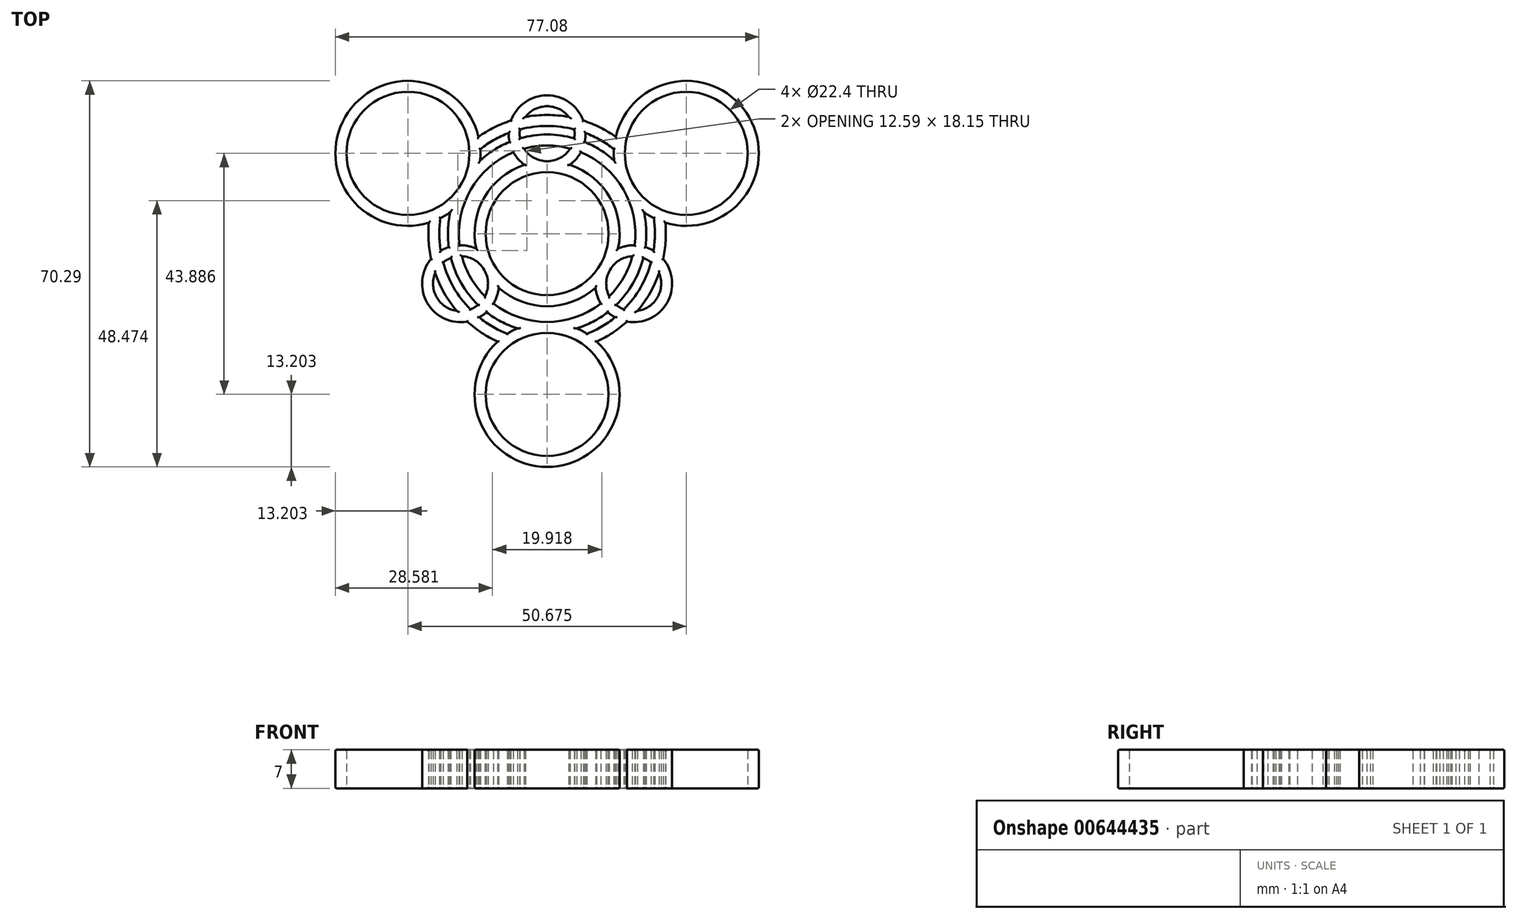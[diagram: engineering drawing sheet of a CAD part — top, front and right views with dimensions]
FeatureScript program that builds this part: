
annotation { "Feature Type Name" : "Feature", "Feature Type Description" : "" }
export const myFeature = defineFeature(function(context is Context, id is Id, definition is map)
    precondition{}
    {
        {
            var Q0;
            Q0=qCreatedBy(makeId("Top.planeOp"),FACE);
            var sketch = newSketch(context, id + "F0", { "sketchPlane" : qUnion([Q0])});
            skCircle(sketch, "E0", {"center": v(0, 0) * mm, "radius": 11.2 * mm});
            skArc(sketch, "E1.0", {"start": v(-4.12, 12.54) * mm, "mid": v(-11.43, 6.6) * mm, "end": v(-12.92, -2.7) * mm});
            skArc(sketch, "E2", {"start": v(4.93, 17.37) * mm, "mid": v(5, 18.18) * mm, "end": v(4.94, 18.99) * mm});
            skArc(sketch, "E3.0", {"start": v(4.12, 12.54) * mm, "mid": v(5.26, 13.58) * mm, "end": v(6.14, 14.84) * mm});
            skPoint(sketch, "E4", {"position": v(0, 11.2) * mm});
            skArc(sketch, "E5.1.0", {"start": v(8.8, -9.84) * mm, "mid": v(9.13, -11.34) * mm, "end": v(9.78, -12.74) * mm});
            skArc(sketch, "E5.1.1", {"start": v(12.58, -12.96) * mm, "mid": v(13.24, -13.42) * mm, "end": v(13.97, -13.77) * mm});
            skArc(sketch, "E5.2.0", {"start": v(-12.92, -2.7) * mm, "mid": v(-14.39, -2.24) * mm, "end": v(-15.92, -2.1) * mm});
            skArc(sketch, "E5.2.1", {"start": v(-17.5, -4.42) * mm, "mid": v(-18.24, -4.76) * mm, "end": v(-18.91, -5.22) * mm});
            skLineSegment(sketch, "E5.anchor1", {"start": v(0, 0) * mm, "end": v(0, 18.2) * mm, "construction": true});
            skLineSegment(sketch, "E5.anchor2", {"start": v(0, 0) * mm, "end": v(-15.76, -9.1) * mm, "construction": true});
            skArc(sketch, "E6", {"start": v(-15.52, -4.1) * mm, "mid": v(-13.9, -8.03) * mm, "end": v(-11.32, -11.4) * mm});
            skArc(sketch, "E7.0", {"start": v(12.2, 13.3) * mm, "mid": v(9.67, 15.25) * mm, "end": v(6.84, 16.71) * mm});
            skArc(sketch, "E8.trimOffspring", {"start": v(12.92, -2.7) * mm, "mid": v(11.43, 6.6) * mm, "end": v(4.12, 12.54) * mm});
            skArc(sketch, "E9.trimOffspring", {"start": v(-8.8, -9.84) * mm, "mid": v(0, -13.2) * mm, "end": v(8.8, -9.84) * mm});
            skArc(sketch, "E10.trimOffspring", {"start": v(6.84, 16.71) * mm, "mid": v(6.97, 17.51) * mm, "end": v(7, 18.33) * mm});
            skArc(sketch, "E11.trimOffspring", {"start": v(-4.2, 15.5) * mm, "mid": v(0, 13.2) * mm, "end": v(4.2, 15.5) * mm});
            skArc(sketch, "E12.trimOffspring", {"start": v(-6.14, 14.84) * mm, "mid": v(-5.26, 13.58) * mm, "end": v(-4.12, 12.54) * mm});
            skArc(sketch, "E13.trimOffspring", {"start": v(-17.9, -2.43) * mm, "mid": v(-18.65, -2.72) * mm, "end": v(-19.37, -3.1) * mm});
            skArc(sketch, "E14.trimOffspring", {"start": v(-9.78, -12.74) * mm, "mid": v(-9.13, -11.34) * mm, "end": v(-8.8, -9.84) * mm});
            skArc(sketch, "E15.trimOffspring", {"start": v(-11.32, -11.4) * mm, "mid": v(-11.43, -6.6) * mm, "end": v(-15.52, -4.1) * mm});
            skArc(sketch, "E16.trimOffspring", {"start": v(11.05, -14.28) * mm, "mid": v(11.68, -14.8) * mm, "end": v(12.37, -15.22) * mm});
            skArc(sketch, "E17.trimOffspring", {"start": v(15.52, -4.1) * mm, "mid": v(11.43, -6.6) * mm, "end": v(11.32, -11.4) * mm});
            skArc(sketch, "E18.trimOffspring", {"start": v(15.92, -2.1) * mm, "mid": v(14.39, -2.24) * mm, "end": v(12.92, -2.7) * mm});
            skCircle(sketch, "E19", {"center": v(25.34, 14.63) * mm, "radius": 11.2 * mm});
            skArc(sketch, "E20.0", {"start": v(21.53, 2) * mm, "mid": v(36.77, 21.23) * mm, "end": v(12.49, 17.65) * mm});
            skLineSegment(sketch, "E21", {"start": v(25.34, 14.63) * mm, "end": v(25.34, 1.43) * mm, "construction": true});
            skLineSegment(sketch, "E22", {"start": v(25.34, 14.63) * mm, "end": v(13.9, 8.03) * mm, "construction": true});
            skLineSegment(sketch, "E23", {"start": v(0, 0) * mm, "end": v(13.9, 8.03) * mm, "construction": true});
            skCircle(sketch, "E24.1.0", {"center": v(-25.34, 14.63) * mm, "radius": 11.2 * mm});
            skArc(sketch, "E24.1.1", {"start": v(-19.41, 2.83) * mm, "mid": v(-18.5, 3.34) * mm, "end": v(-17.63, 3.91) * mm});
            skCircle(sketch, "E24.2.0", {"center": v(0, -29.26) * mm, "radius": 11.2 * mm});
            skArc(sketch, "E24.2.1", {"start": v(7.25, -18.23) * mm, "mid": v(6.36, -17.69) * mm, "end": v(5.42, -17.22) * mm});
            skArc(sketch, "E25", {"start": v(12.16, 15.4) * mm, "mid": v(9.7, 17.06) * mm, "end": v(7, 18.33) * mm});
            skArc(sketch, "E26.0", {"start": v(12.49, 17.65) * mm, "mid": v(9.65, 19.35) * mm, "end": v(6.58, 20.6) * mm});
            skArc(sketch, "E27.trimOffspring", {"start": v(12.16, 15.4) * mm, "mid": v(12.14, 14.35) * mm, "end": v(12.2, 13.3) * mm});
            skArc(sketch, "E28.trimOffspring", {"start": v(17.63, 3.91) * mm, "mid": v(18.5, 3.34) * mm, "end": v(19.41, 2.83) * mm});
            skArc(sketch, "E29.trimOffspring", {"start": v(19.37, -3.1) * mm, "mid": v(18.65, -2.72) * mm, "end": v(17.9, -2.43) * mm});
            skArc(sketch, "E30.trimOffspring", {"start": v(18.91, -5.22) * mm, "mid": v(18.24, -4.76) * mm, "end": v(17.5, -4.42) * mm});
            skArc(sketch, "E31.trimOffspring", {"start": v(16.42, -14.06) * mm, "mid": v(20.1, -11.6) * mm, "end": v(20.38, -7.2) * mm});
            skArc(sketch, "E32.trimOffspring", {"start": v(14.54, -16) * mm, "mid": v(21.82, -12.6) * mm, "end": v(21.12, -4.6) * mm});
            skArc(sketch, "E33.trimOffspring", {"start": v(6.58, 20.6) * mm, "mid": v(0, 25.2) * mm, "end": v(-6.58, 20.6) * mm});
            skArc(sketch, "E34.trimOffspring", {"start": v(3.96, 21.25) * mm, "mid": v(0, 23.2) * mm, "end": v(-3.96, 21.25) * mm});
            skArc(sketch, "E35.trimOffspring", {"start": v(-4.94, 18.99) * mm, "mid": v(-5, 18.18) * mm, "end": v(-4.93, 17.37) * mm});
            skArc(sketch, "E36.trimOffspring", {"start": v(-7, 18.33) * mm, "mid": v(-6.97, 17.51) * mm, "end": v(-6.84, 16.71) * mm});
            skArc(sketch, "E37.trimOffspring", {"start": v(-12.37, -15.22) * mm, "mid": v(-11.68, -14.8) * mm, "end": v(-11.05, -14.28) * mm});
            skArc(sketch, "E38.trimOffspring", {"start": v(-13.97, -13.77) * mm, "mid": v(-13.24, -13.42) * mm, "end": v(-12.58, -12.96) * mm});
            skArc(sketch, "E39.trimOffspring", {"start": v(-20.38, -7.2) * mm, "mid": v(-20.1, -11.6) * mm, "end": v(-16.42, -14.06) * mm});
            skArc(sketch, "E40.trimOffspring", {"start": v(-21.12, -4.6) * mm, "mid": v(-21.82, -12.6) * mm, "end": v(-14.54, -16) * mm});
            skArc(sketch, "E41.trimOffspring", {"start": v(-21.53, 2) * mm, "mid": v(-21.58, -1.32) * mm, "end": v(-21.12, -4.6) * mm});
            skArc(sketch, "E42.trimOffspring", {"start": v(-19.41, 2.83) * mm, "mid": v(-19.62, -0.14) * mm, "end": v(-19.37, -3.1) * mm});
            skArc(sketch, "E43.trimOffspring", {"start": v(9.04, -19.64) * mm, "mid": v(11.93, -18.03) * mm, "end": v(14.54, -16) * mm});
            skArc(sketch, "E44.trimOffspring", {"start": v(7.25, -18.23) * mm, "mid": v(9.93, -16.92) * mm, "end": v(12.37, -15.22) * mm});
            skArc(sketch, "E45.trimOffspring", {"start": v(5.42, -17.22) * mm, "mid": v(8.37, -16) * mm, "end": v(11.05, -14.28) * mm});
            skArc(sketch, "E46.trimOffspring", {"start": v(-9.04, -19.64) * mm, "mid": v(0, -42.46) * mm, "end": v(9.04, -19.64) * mm});
            skArc(sketch, "E47.trimOffspring", {"start": v(-5.42, -17.22) * mm, "mid": v(-6.36, -17.69) * mm, "end": v(-7.25, -18.23) * mm});
            skArc(sketch, "E48.trimOffspring", {"start": v(-12.49, 17.65) * mm, "mid": v(-36.77, 21.23) * mm, "end": v(-21.53, 2) * mm});
            skArc(sketch, "E49.trimOffspring", {"start": v(-17.63, 3.91) * mm, "mid": v(-18.04, 0.75) * mm, "end": v(-17.9, -2.43) * mm});
            skArc(sketch, "E50.trimOffspring", {"start": v(-12.2, 13.3) * mm, "mid": v(-12.14, 14.35) * mm, "end": v(-12.16, 15.4) * mm});
            skArc(sketch, "E51.trimOffspring", {"start": v(-17.5, -4.42) * mm, "mid": v(-15.64, -9.03) * mm, "end": v(-12.58, -12.96) * mm});
            skArc(sketch, "E52.trimOffspring", {"start": v(-18.91, -5.22) * mm, "mid": v(-16.99, -9.8) * mm, "end": v(-13.97, -13.77) * mm});
            skArc(sketch, "E53.trimOffspring", {"start": v(-20.38, -7.2) * mm, "mid": v(-18.72, -10.8) * mm, "end": v(-16.42, -14.06) * mm});
            skArc(sketch, "E54.trimOffspring", {"start": v(-14.54, -16) * mm, "mid": v(-11.93, -18.03) * mm, "end": v(-9.04, -19.64) * mm});
            skArc(sketch, "E55.trimOffspring", {"start": v(-12.37, -15.22) * mm, "mid": v(-9.93, -16.92) * mm, "end": v(-7.25, -18.23) * mm});
            skArc(sketch, "E56.trimOffspring", {"start": v(-11.05, -14.28) * mm, "mid": v(-8.37, -16) * mm, "end": v(-5.42, -17.22) * mm});
            skArc(sketch, "E57.trimOffspring", {"start": v(-9.78, -12.74) * mm, "mid": v(0, -16.06) * mm, "end": v(9.78, -12.74) * mm});
            skArc(sketch, "E58.trimOffspring", {"start": v(11.32, -11.4) * mm, "mid": v(13.9, -8.03) * mm, "end": v(15.52, -4.1) * mm});
            skArc(sketch, "E59.trimOffspring", {"start": v(12.58, -12.96) * mm, "mid": v(15.64, -9.03) * mm, "end": v(17.5, -4.42) * mm});
            skArc(sketch, "E60.trimOffspring", {"start": v(13.97, -13.77) * mm, "mid": v(16.99, -9.8) * mm, "end": v(18.91, -5.22) * mm});
            skArc(sketch, "E61.trimOffspring", {"start": v(16.42, -14.06) * mm, "mid": v(18.72, -10.8) * mm, "end": v(20.38, -7.2) * mm});
            skArc(sketch, "E62.trimOffspring", {"start": v(21.12, -4.6) * mm, "mid": v(21.58, -1.32) * mm, "end": v(21.53, 2) * mm});
            skArc(sketch, "E63.trimOffspring", {"start": v(19.37, -3.1) * mm, "mid": v(19.62, -0.14) * mm, "end": v(19.41, 2.83) * mm});
            skArc(sketch, "E64.trimOffspring", {"start": v(17.9, -2.43) * mm, "mid": v(18.04, 0.75) * mm, "end": v(17.63, 3.91) * mm});
            skArc(sketch, "E65.trimOffspring", {"start": v(15.92, -2.1) * mm, "mid": v(13.9, 8.03) * mm, "end": v(6.14, 14.84) * mm});
            skArc(sketch, "E66.trimOffspring", {"start": v(-6.14, 14.84) * mm, "mid": v(-13.9, 8.03) * mm, "end": v(-15.92, -2.1) * mm});
            skArc(sketch, "E67.trimOffspring", {"start": v(-6.84, 16.71) * mm, "mid": v(-9.67, 15.25) * mm, "end": v(-12.2, 13.3) * mm});
            skArc(sketch, "E68.trimOffspring", {"start": v(-7, 18.33) * mm, "mid": v(-9.7, 17.06) * mm, "end": v(-12.16, 15.4) * mm});
            skArc(sketch, "E69.trimOffspring", {"start": v(-6.58, 20.6) * mm, "mid": v(-9.65, 19.35) * mm, "end": v(-12.49, 17.65) * mm});
            skArc(sketch, "E70.trimOffspring", {"start": v(3.96, 21.25) * mm, "mid": v(0, 21.62) * mm, "end": v(-3.96, 21.25) * mm});
            skArc(sketch, "E71.trimOffspring", {"start": v(4.94, 18.99) * mm, "mid": v(0, 19.62) * mm, "end": v(-4.94, 18.99) * mm});
            skArc(sketch, "E72.trimOffspring", {"start": v(4.93, 17.37) * mm, "mid": v(0, 18.06) * mm, "end": v(-4.93, 17.37) * mm});
            skArc(sketch, "E73.trimOffspring", {"start": v(4.2, 15.5) * mm, "mid": v(0, 16.06) * mm, "end": v(-4.2, 15.5) * mm});
            skSolve(sketch);
        }
        {
            var Q0;
            Q0=makeQuery(id+"F0.imprint","IMPRINT",FACE,{"disambiguationData":[TD([[makeQuery(id+"F0.imprint","IMPRINT",EDGE,{"derivedFrom":sQuery(id+"F0.wireOp",EDGE,"E0")}),-1.0]])]});
            extrude(context, id + "F1", {"entities" : qUnion([Q0]), "depth" : 7 * mm, "offsetDistance" : 25 * mm});
        }
        {
            var Q0;
            Q0=makeQuery(id+"F1.opExtrude","CAP_FACE",FACE,{"disambiguationData":[OSD([sQuery(id+"F0.wireOp",EDGE,"E0"),sQuery(id+"F0.wireOp",EDGE,"E1.0"),sQuery(id+"F0.wireOp",EDGE,"E2"),sQuery(id+"F0.wireOp",EDGE,"E3.0"),sQuery(id+"F0.wireOp",EDGE,"E5.1.0"),sQuery(id+"F0.wireOp",EDGE,"E5.1.1"),sQuery(id+"F0.wireOp",EDGE,"E5.2.0"),sQuery(id+"F0.wireOp",EDGE,"E5.2.1"),sQuery(id+"F0.wireOp",EDGE,"E6"),sQuery(id+"F0.wireOp",EDGE,"E7.0"),sQuery(id+"F0.wireOp",EDGE,"E8.trimOffspring"),sQuery(id+"F0.wireOp",EDGE,"E9.trimOffspring"),sQuery(id+"F0.wireOp",EDGE,"E10.trimOffspring"),sQuery(id+"F0.wireOp",EDGE,"E11.trimOffspring"),sQuery(id+"F0.wireOp",EDGE,"E12.trimOffspring"),sQuery(id+"F0.wireOp",EDGE,"E13.trimOffspring"),sQuery(id+"F0.wireOp",EDGE,"E14.trimOffspring"),sQuery(id+"F0.wireOp",EDGE,"E15.trimOffspring"),sQuery(id+"F0.wireOp",EDGE,"E16.trimOffspring"),sQuery(id+"F0.wireOp",EDGE,"E17.trimOffspring"),sQuery(id+"F0.wireOp",EDGE,"E18.trimOffspring"),sQuery(id+"F0.wireOp",EDGE,"E19"),sQuery(id+"F0.wireOp",EDGE,"E20.0"),sQuery(id+"F0.wireOp",EDGE,"E24.1.0"),sQuery(id+"F0.wireOp",EDGE,"E24.1.1"),sQuery(id+"F0.wireOp",EDGE,"E24.2.0"),sQuery(id+"F0.wireOp",EDGE,"E24.2.1"),sQuery(id+"F0.wireOp",EDGE,"E25"),sQuery(id+"F0.wireOp",EDGE,"E26.0"),sQuery(id+"F0.wireOp",EDGE,"E27.trimOffspring"),sQuery(id+"F0.wireOp",EDGE,"E28.trimOffspring"),sQuery(id+"F0.wireOp",EDGE,"E29.trimOffspring"),sQuery(id+"F0.wireOp",EDGE,"E30.trimOffspring"),sQuery(id+"F0.wireOp",EDGE,"E31.trimOffspring"),sQuery(id+"F0.wireOp",EDGE,"E32.trimOffspring"),sQuery(id+"F0.wireOp",EDGE,"E33.trimOffspring"),sQuery(id+"F0.wireOp",EDGE,"E34.trimOffspring"),sQuery(id+"F0.wireOp",EDGE,"E35.trimOffspring"),sQuery(id+"F0.wireOp",EDGE,"E36.trimOffspring"),sQuery(id+"F0.wireOp",EDGE,"E37.trimOffspring"),sQuery(id+"F0.wireOp",EDGE,"E38.trimOffspring"),sQuery(id+"F0.wireOp",EDGE,"E39.trimOffspring"),sQuery(id+"F0.wireOp",EDGE,"E40.trimOffspring"),sQuery(id+"F0.wireOp",EDGE,"E41.trimOffspring"),sQuery(id+"F0.wireOp",EDGE,"E42.trimOffspring"),sQuery(id+"F0.wireOp",EDGE,"E43.trimOffspring"),sQuery(id+"F0.wireOp",EDGE,"E44.trimOffspring"),sQuery(id+"F0.wireOp",EDGE,"E45.trimOffspring"),sQuery(id+"F0.wireOp",EDGE,"E46.trimOffspring"),sQuery(id+"F0.wireOp",EDGE,"E47.trimOffspring"),sQuery(id+"F0.wireOp",EDGE,"E48.trimOffspring"),sQuery(id+"F0.wireOp",EDGE,"E49.trimOffspring"),sQuery(id+"F0.wireOp",EDGE,"E50.trimOffspring"),sQuery(id+"F0.wireOp",EDGE,"E51.trimOffspring"),sQuery(id+"F0.wireOp",EDGE,"E52.trimOffspring"),sQuery(id+"F0.wireOp",EDGE,"E53.trimOffspring"),sQuery(id+"F0.wireOp",EDGE,"E54.trimOffspring"),sQuery(id+"F0.wireOp",EDGE,"E55.trimOffspring"),sQuery(id+"F0.wireOp",EDGE,"E56.trimOffspring"),sQuery(id+"F0.wireOp",EDGE,"E57.trimOffspring"),sQuery(id+"F0.wireOp",EDGE,"E58.trimOffspring"),sQuery(id+"F0.wireOp",EDGE,"E59.trimOffspring"),sQuery(id+"F0.wireOp",EDGE,"E60.trimOffspring"),sQuery(id+"F0.wireOp",EDGE,"E61.trimOffspring"),sQuery(id+"F0.wireOp",EDGE,"E62.trimOffspring"),sQuery(id+"F0.wireOp",EDGE,"E63.trimOffspring"),sQuery(id+"F0.wireOp",EDGE,"E64.trimOffspring"),sQuery(id+"F0.wireOp",EDGE,"E65.trimOffspring"),sQuery(id+"F0.wireOp",EDGE,"E66.trimOffspring"),sQuery(id+"F0.wireOp",EDGE,"E67.trimOffspring"),sQuery(id+"F0.wireOp",EDGE,"E68.trimOffspring"),sQuery(id+"F0.wireOp",EDGE,"E69.trimOffspring"),sQuery(id+"F0.wireOp",EDGE,"E70.trimOffspring"),sQuery(id+"F0.wireOp",EDGE,"E71.trimOffspring"),sQuery(id+"F0.wireOp",EDGE,"E72.trimOffspring"),sQuery(id+"F0.wireOp",EDGE,"E73.trimOffspring")])],"isStart":false});
            var Q1;
            Q1=makeQuery(id+"F1.opExtrude","CAP_FACE",FACE,{"disambiguationData":[OSD([sQuery(id+"F0.wireOp",EDGE,"E0"),sQuery(id+"F0.wireOp",EDGE,"E1.0"),sQuery(id+"F0.wireOp",EDGE,"E2"),sQuery(id+"F0.wireOp",EDGE,"E3.0"),sQuery(id+"F0.wireOp",EDGE,"E5.1.0"),sQuery(id+"F0.wireOp",EDGE,"E5.1.1"),sQuery(id+"F0.wireOp",EDGE,"E5.2.0"),sQuery(id+"F0.wireOp",EDGE,"E5.2.1"),sQuery(id+"F0.wireOp",EDGE,"E6"),sQuery(id+"F0.wireOp",EDGE,"E7.0"),sQuery(id+"F0.wireOp",EDGE,"E8.trimOffspring"),sQuery(id+"F0.wireOp",EDGE,"E9.trimOffspring"),sQuery(id+"F0.wireOp",EDGE,"E10.trimOffspring"),sQuery(id+"F0.wireOp",EDGE,"E11.trimOffspring"),sQuery(id+"F0.wireOp",EDGE,"E12.trimOffspring"),sQuery(id+"F0.wireOp",EDGE,"E13.trimOffspring"),sQuery(id+"F0.wireOp",EDGE,"E14.trimOffspring"),sQuery(id+"F0.wireOp",EDGE,"E15.trimOffspring"),sQuery(id+"F0.wireOp",EDGE,"E16.trimOffspring"),sQuery(id+"F0.wireOp",EDGE,"E17.trimOffspring"),sQuery(id+"F0.wireOp",EDGE,"E18.trimOffspring"),sQuery(id+"F0.wireOp",EDGE,"E19"),sQuery(id+"F0.wireOp",EDGE,"E20.0"),sQuery(id+"F0.wireOp",EDGE,"E24.1.0"),sQuery(id+"F0.wireOp",EDGE,"E24.1.1"),sQuery(id+"F0.wireOp",EDGE,"E24.2.0"),sQuery(id+"F0.wireOp",EDGE,"E24.2.1"),sQuery(id+"F0.wireOp",EDGE,"E25"),sQuery(id+"F0.wireOp",EDGE,"E26.0"),sQuery(id+"F0.wireOp",EDGE,"E27.trimOffspring"),sQuery(id+"F0.wireOp",EDGE,"E28.trimOffspring"),sQuery(id+"F0.wireOp",EDGE,"E29.trimOffspring"),sQuery(id+"F0.wireOp",EDGE,"E30.trimOffspring"),sQuery(id+"F0.wireOp",EDGE,"E31.trimOffspring"),sQuery(id+"F0.wireOp",EDGE,"E32.trimOffspring"),sQuery(id+"F0.wireOp",EDGE,"E33.trimOffspring"),sQuery(id+"F0.wireOp",EDGE,"E34.trimOffspring"),sQuery(id+"F0.wireOp",EDGE,"E35.trimOffspring"),sQuery(id+"F0.wireOp",EDGE,"E36.trimOffspring"),sQuery(id+"F0.wireOp",EDGE,"E37.trimOffspring"),sQuery(id+"F0.wireOp",EDGE,"E38.trimOffspring"),sQuery(id+"F0.wireOp",EDGE,"E39.trimOffspring"),sQuery(id+"F0.wireOp",EDGE,"E40.trimOffspring"),sQuery(id+"F0.wireOp",EDGE,"E41.trimOffspring"),sQuery(id+"F0.wireOp",EDGE,"E42.trimOffspring"),sQuery(id+"F0.wireOp",EDGE,"E43.trimOffspring"),sQuery(id+"F0.wireOp",EDGE,"E44.trimOffspring"),sQuery(id+"F0.wireOp",EDGE,"E45.trimOffspring"),sQuery(id+"F0.wireOp",EDGE,"E46.trimOffspring"),sQuery(id+"F0.wireOp",EDGE,"E47.trimOffspring"),sQuery(id+"F0.wireOp",EDGE,"E48.trimOffspring"),sQuery(id+"F0.wireOp",EDGE,"E49.trimOffspring"),sQuery(id+"F0.wireOp",EDGE,"E50.trimOffspring"),sQuery(id+"F0.wireOp",EDGE,"E51.trimOffspring"),sQuery(id+"F0.wireOp",EDGE,"E52.trimOffspring"),sQuery(id+"F0.wireOp",EDGE,"E53.trimOffspring"),sQuery(id+"F0.wireOp",EDGE,"E54.trimOffspring"),sQuery(id+"F0.wireOp",EDGE,"E55.trimOffspring"),sQuery(id+"F0.wireOp",EDGE,"E56.trimOffspring"),sQuery(id+"F0.wireOp",EDGE,"E57.trimOffspring"),sQuery(id+"F0.wireOp",EDGE,"E58.trimOffspring"),sQuery(id+"F0.wireOp",EDGE,"E59.trimOffspring"),sQuery(id+"F0.wireOp",EDGE,"E60.trimOffspring"),sQuery(id+"F0.wireOp",EDGE,"E61.trimOffspring"),sQuery(id+"F0.wireOp",EDGE,"E62.trimOffspring"),sQuery(id+"F0.wireOp",EDGE,"E63.trimOffspring"),sQuery(id+"F0.wireOp",EDGE,"E64.trimOffspring"),sQuery(id+"F0.wireOp",EDGE,"E65.trimOffspring"),sQuery(id+"F0.wireOp",EDGE,"E66.trimOffspring"),sQuery(id+"F0.wireOp",EDGE,"E67.trimOffspring"),sQuery(id+"F0.wireOp",EDGE,"E68.trimOffspring"),sQuery(id+"F0.wireOp",EDGE,"E69.trimOffspring"),sQuery(id+"F0.wireOp",EDGE,"E70.trimOffspring"),sQuery(id+"F0.wireOp",EDGE,"E71.trimOffspring"),sQuery(id+"F0.wireOp",EDGE,"E72.trimOffspring"),sQuery(id+"F0.wireOp",EDGE,"E73.trimOffspring")])],"isStart":true});
            fillet(context, id + "F2", {"entities" : qUnion([Q0, Q1]), "radius" : 0.2 * mm, "tangentPropagation" : true, "allowEdgeOverflow" : false});
        }
    });
